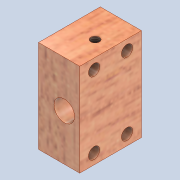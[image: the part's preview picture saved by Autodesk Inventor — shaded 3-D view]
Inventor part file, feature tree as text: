
AUTODESK INVENTOR PART (.ipt)
format: ipt  version: 2020 (Build 240168000, 168)  size: 166,400 bytes
history: native  units: mm
features: sketch x4, extrude x3, pattern_linear x1, hole x1
ambient origin geometry x8: Origin, YZ Plane, XZ Plane, XY Plane, X Axis, Y Axis, Z Axis, Center Point
bodies: Solid1 (feature_tree)
feature tree (9):
  extrude  "Extrusion1"  Depth=45.0mm
  extrude  "Extrusion2"  Depth=10.0mm
  extrude  "Extrusion3"  TaperAngle=0.0deg  [1 undecoded]
  pattern_linear  "Rectangular Pattern1"  Spacing1=5.5mm  [1 undecoded]
  hole  "Hole1"  [1 undecoded]
  sketch  "Sketch1"  dims[d0=20.0mm d1=45.0mm]
  sketch  "Sketch3"  dims[d2=30.0mm d3=0.0mm d4=10.0mm]
  sketch  "Sketch4"  dims[d5=7.5mm d6=0.0mm d7=0.0mm]
  sketch  "Sketch5"  dims[d8=5.5mm d9=5.5mm d10=7.0mm d11=5.0mm d12=5.0mm d13=7.0mm d14=0.0mm d15=0.0mm d16=35.0mm d17=16.0mm d18=20.0mm d20=16.0mm d21=20.0mm d23=35.0mm d24=4.134mm d25=45.0mm d26=4.0mm d27=2.0mm d28=90.0deg d29=8.0mm d30=20.594885mm d38=12.5mm]
note: 3 required parameter values undecoded (feature->parameter linkage not recoverable at this tier; creation-order binding heuristic only, values carry confidence <= 0.55)
